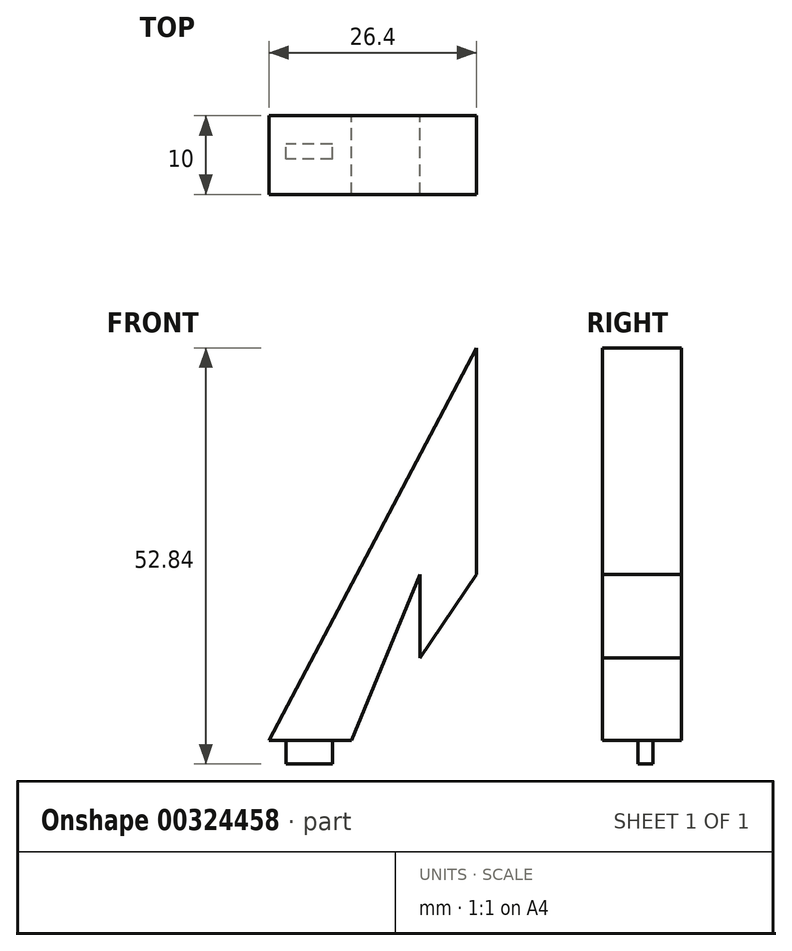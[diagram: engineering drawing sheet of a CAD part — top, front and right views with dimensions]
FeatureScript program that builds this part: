
annotation { "Feature Type Name" : "Feature", "Feature Type Description" : "" }
export const myFeature = defineFeature(function(context is Context, id is Id, definition is map)
    precondition{}
    {
        {
            var Q0;
            Q0=qCreatedBy(makeId("Front.planeOp"),FACE);
            var sketch = newSketch(context, id + "F0", { "sketchPlane" : qUnion([Q0])});
            skLineSegment(sketch, "E0", {"start": v(-26.4, 0) * mm, "end": v(0, 49.84) * mm});
            skLineSegment(sketch, "E1", {"start": v(0, 49.84) * mm, "end": v(0, 21.04) * mm});
            skLineSegment(sketch, "E2", {"start": v(0, 21.04) * mm, "end": v(-7.22, 10.47) * mm});
            skLineSegment(sketch, "E3", {"start": v(-7.22, 10.47) * mm, "end": v(-7.22, 21.07) * mm});
            skLineSegment(sketch, "E4", {"start": v(-7.22, 21.07) * mm, "end": v(-15.93, 0) * mm});
            skLineSegment(sketch, "E5", {"start": v(-15.93, 0) * mm, "end": v(-26.4, 0) * mm});
            skSolve(sketch);
        }
        {
            var Q0;
            Q0 = qSketchRegion(id + "F0", true);
            extrude(context, id + "F1", {"entities" : qUnion([Q0]), "depth" : 10 * mm});
        }
        {
            var Q0;
            Q0=makeQuery(id+"F1.opExtrude","SWEPT_FACE",FACE,{"disambiguationData":[OSD([sQuery(id+"F0.wireOp",EDGE,"E5")])]});
            var sketch = newSketch(context, id + "F2", { "sketchPlane" : qUnion([Q0])});
            skSolve(sketch);
        }
        {
            var Q0;
            {var subQ0=sQuery(id+"F0.wireOp",EDGE,"E5");Q0=makeQuery(id+"F2.imprint","IMPRINT",FACE,{"disambiguationData":[TD([[makeQuery(id+"F2.imprint","IMPRINT",EDGE,{"derivedFrom":makeQuery(id+"F1.opExtrude","CAP_EDGE",EDGE,{"disambiguationData":[OSD([subQ0])],"isStart":true})}),-1.0]])]});}
            var sketch = newSketch(context, id + "F3", { "sketchPlane" : qUnion([Q0])});
            skLineSegment(sketch, "E6.bottom", {"start": v(-18.34, 5.51) * mm, "end": v(-24.22, 5.51) * mm});
            skLineSegment(sketch, "E6.top", {"start": v(-18.34, 3.62) * mm, "end": v(-24.22, 3.62) * mm});
            skLineSegment(sketch, "E6.left", {"start": v(-18.34, 5.51) * mm, "end": v(-18.34, 3.62) * mm});
            skLineSegment(sketch, "E6.right", {"start": v(-24.22, 5.51) * mm, "end": v(-24.22, 3.62) * mm});
            skPoint(sketch, "E6.middle", {"position": v(-21.28, 4.56) * mm});
            skSolve(sketch);
        }
        {
            var Q0;
            Q0 = qSketchRegion(id + "F3", true);
            extrude(context, id + "F4", {"entities" : qUnion([Q0]), "operationType" : NewBodyOperationType.ADD, "depth" : 3 * mm});
        }
    });
